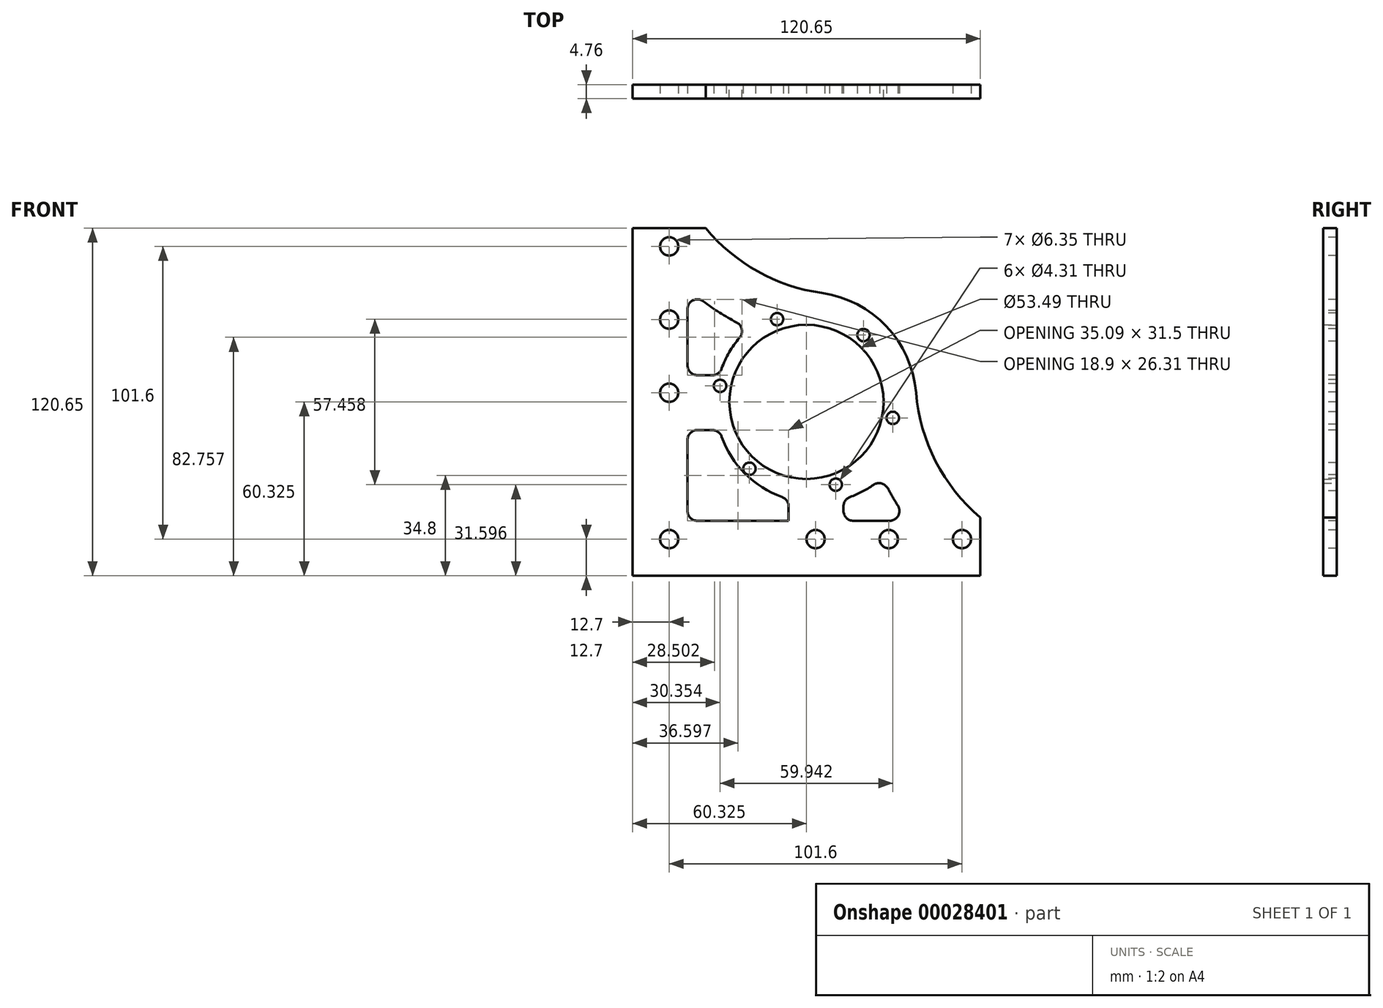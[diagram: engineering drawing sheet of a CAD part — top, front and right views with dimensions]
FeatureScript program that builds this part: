
annotation { "Feature Type Name" : "Feature", "Feature Type Description" : "" }
export const myFeature = defineFeature(function(context is Context, id is Id, definition is map)
    precondition{}
    {
        {
            var Q0;
            Q0=qCreatedBy(makeId("Front.planeOp"),FACE);
            var sketch = newSketch(context, id + "F0", { "sketchPlane" : qUnion([Q0])});
            skLineSegment(sketch, "E0.bottom", {"start": v(0, 0) * mm, "end": v(120.65, 0) * mm});
            skLineSegment(sketch, "E0.top", {"start": v(0, 120.65) * mm, "end": v(25.4, 120.65) * mm});
            skLineSegment(sketch, "E0.left", {"start": v(0, 0) * mm, "end": v(0, 120.65) * mm});
            skLineSegment(sketch, "E0.right", {"start": v(120.65, 0) * mm, "end": v(120.65, 20.24) * mm});
            skCircle(sketch, "E1", {"center": v(60.32, 60.33) * mm, "radius": 26.75 * mm});
            skArc(sketch, "E2", {"start": v(98.37, 63.48) * mm, "mid": v(88.07, 86.55) * mm, "end": v(65.62, 98.13) * mm});
            skArc(sketch, "E3", {"start": v(25.4, 120.65) * mm, "mid": v(43.4, 105.61) * mm, "end": v(65.62, 98.13) * mm});
            skArc(sketch, "E4", {"start": v(98.37, 63.48) * mm, "mid": v(105.2, 39.64) * mm, "end": v(120.65, 20.24) * mm});
            skSolve(sketch);
        }
        {
            var Q0;
            Q0=makeQuery(id+"F0.imprint","IMPRINT",FACE,{"disambiguationData":[TD([[makeQuery(id+"F0.imprint","IMPRINT",EDGE,{"derivedFrom":sQuery(id+"F0.wireOp",EDGE,"E0.bottom")}),1.0]])]});
            var Q1;
            Q1=makeQuery(id+"F0.imprint","IMPRINT",FACE,{"disambiguationData":[TD([[makeQuery(id+"F0.imprint","IMPRINT",EDGE,{"derivedFrom":sQuery(id+"F0.wireOp",EDGE,"E1")}),-1.0]])]});
            extrude(context, id + "F1", {"entities" : qUnion([Q0, Q1]), "depth" : 4.76 * mm});
        }
        {
            var Q0;
            Q0=makeQuery(id+"F1.opExtrude","CAP_FACE",FACE,{"disambiguationData":[OSD([sQuery(id+"F0.wireOp",EDGE,"E0.bottom"),sQuery(id+"F0.wireOp",EDGE,"E0.top"),sQuery(id+"F0.wireOp",EDGE,"E0.left"),sQuery(id+"F0.wireOp",EDGE,"E0.right"),sQuery(id+"F0.wireOp",EDGE,"E1"),sQuery(id+"F0.wireOp",EDGE,"E2"),sQuery(id+"F0.wireOp",EDGE,"E3"),sQuery(id+"F0.wireOp",EDGE,"E4")])],"isStart":false});
            var sketch = newSketch(context, id + "F2", { "sketchPlane" : qUnion([Q0])});
            skLineSegment(sketch, "E5.0", {"start": v(17.11, 101.6) * mm, "end": v(19.05, 101.6) * mm});
            skLineSegment(sketch, "E5.1", {"start": v(19.05, 19.05) * mm, "end": v(19.05, 50.55) * mm});
            skLineSegment(sketch, "E5.2", {"start": v(19.05, 19.05) * mm, "end": v(54.14, 19.05) * mm});
            skArc(sketch, "E5.3", {"start": v(86.76, 34) * mm, "mid": v(90.84, 26.3) * mm, "end": v(95.72, 19.05) * mm});
            skArc(sketch, "E5.5", {"start": v(17.11, 101.6) * mm, "mid": v(28.02, 92.74) * mm, "end": v(40.27, 85.86) * mm});
            skArc(sketch, "E6", {"start": v(73.2, 26.58) * mm, "mid": v(80.4, 29.53) * mm, "end": v(86.76, 34) * mm});
            skLineSegment(sketch, "E7.bottom", {"start": v(19.05, 69.6) * mm, "end": v(30.17, 69.6) * mm});
            skLineSegment(sketch, "E7.top", {"start": v(19.05, 50.55) * mm, "end": v(30.17, 50.55) * mm});
            skLineSegment(sketch, "E8.left", {"start": v(54.14, 26.58) * mm, "end": v(54.14, 19.05) * mm});
            skLineSegment(sketch, "E8.right", {"start": v(73.2, 26.58) * mm, "end": v(73.2, 19.05) * mm});
            skLineSegment(sketch, "E9.trimOffspring", {"start": v(19.05, 69.6) * mm, "end": v(19.05, 101.6) * mm});
            skArc(sketch, "E10.trimOffspring", {"start": v(30.17, 50.55) * mm, "mid": v(39.04, 35.45) * mm, "end": v(54.14, 26.58) * mm});
            skLineSegment(sketch, "E11.trimOffspring", {"start": v(73.2, 19.05) * mm, "end": v(95.72, 19.05) * mm});
            skArc(sketch, "E12.trimOffspring", {"start": v(40.27, 85.86) * mm, "mid": v(34.08, 78.44) * mm, "end": v(30.17, 69.6) * mm});
            skLineSegment(sketch, "E13", {"start": v(63.67, 60.08) * mm, "end": v(63.67, -18.33) * mm, "construction": true});
            skLineSegment(sketch, "E14", {"start": v(63.67, 60.08) * mm, "end": v(-21.5, 60.08) * mm, "construction": true});
            skSolve(sketch);
        }
        {
            var Q0;
            {var subQ4=sQuery(id+"F2.wireOp",EDGE,"E7.bottom");Q0=makeQuery(id+"F2.imprint","IMPRINT",FACE,{"disambiguationData":[TD([[makeQuery(id+"F2.imprint","IMPRINT",EDGE,{"derivedFrom":subQ4}),1.0]])]});}
            var Q1;
            Q1=makeQuery(id+"F2.imprint","IMPRINT",FACE,{"disambiguationData":[TD([[makeQuery(id+"F2.imprint","IMPRINT",EDGE,{"derivedFrom":sQuery(id+"F2.wireOp",EDGE,"E5.1")}),-1.0]])]});
            var Q2;
            Q2=makeQuery(id+"F2.imprint","IMPRINT",FACE,{"disambiguationData":[TD([[makeQuery(id+"F2.imprint","IMPRINT",EDGE,{"derivedFrom":sQuery(id+"F2.wireOp",EDGE,"E5.3")}),-1.0]])]});
            extrude(context, id + "F3", {"entities" : qUnion([Q0, Q1, Q2]), "operationType" : NewBodyOperationType.REMOVE, "endBound" : BoundingType.THROUGH_ALL, "oppositeDirection" : true, "depth" : 25.4 * mm});
        }
        {
            var Q0;
            Q0=makeQuery(id+"F3.boolean.opBoolean","COPY",EDGE,{"derivedFrom":makeQuery(id+"F3.opExtrude","SWEPT_EDGE",EDGE,{"disambiguationData":[OSD([sQuery(id+"F2.wireOp",EDGE,"E5.5"),sQuery(id+"F2.wireOp",EDGE,"E9.trimOffspring")])]})});
            var Q1;
            Q1=makeQuery(id+"F3.boolean.opBoolean","COPY",EDGE,{"derivedFrom":makeQuery(id+"F3.opExtrude","SWEPT_EDGE",EDGE,{"disambiguationData":[OSD([sQuery(id+"F2.wireOp",EDGE,"E7.bottom"),sQuery(id+"F2.wireOp",EDGE,"E9.trimOffspring")])]})});
            var Q2;
            Q2=makeQuery(id+"F3.boolean.opBoolean","COPY",EDGE,{"derivedFrom":makeQuery(id+"F3.opExtrude","SWEPT_EDGE",EDGE,{"disambiguationData":[OSD([sQuery(id+"F2.wireOp",EDGE,"E7.bottom"),sQuery(id+"F2.wireOp",EDGE,"E12.trimOffspring")])]})});
            var Q3;
            Q3=makeQuery(id+"F3.boolean.opBoolean","COPY",EDGE,{"derivedFrom":makeQuery(id+"F3.opExtrude","SWEPT_EDGE",EDGE,{"disambiguationData":[OSD([sQuery(id+"F2.wireOp",EDGE,"E5.5"),sQuery(id+"F2.wireOp",EDGE,"E12.trimOffspring")])]})});
            var Q4;
            Q4=makeQuery(id+"F3.boolean.opBoolean","COPY",EDGE,{"derivedFrom":makeQuery(id+"F3.opExtrude","SWEPT_EDGE",EDGE,{"disambiguationData":[OSD([sQuery(id+"F2.wireOp",EDGE,"E8.left"),sQuery(id+"F2.wireOp",EDGE,"E10.trimOffspring")])]})});
            var Q5;
            Q5=makeQuery(id+"F3.boolean.opBoolean","COPY",EDGE,{"derivedFrom":makeQuery(id+"F3.opExtrude","SWEPT_EDGE",EDGE,{"disambiguationData":[OSD([sQuery(id+"F2.wireOp",EDGE,"E7.top"),sQuery(id+"F2.wireOp",EDGE,"E10.trimOffspring")])]})});
            var Q6;
            Q6=makeQuery(id+"F3.boolean.opBoolean","COPY",EDGE,{"derivedFrom":makeQuery(id+"F3.opExtrude","SWEPT_EDGE",EDGE,{"disambiguationData":[OSD([sQuery(id+"F2.wireOp",EDGE,"E5.1"),sQuery(id+"F2.wireOp",EDGE,"E7.top")])]})});
            var Q7;
            Q7=makeQuery(id+"F3.boolean.opBoolean","COPY",EDGE,{"derivedFrom":makeQuery(id+"F3.opExtrude","SWEPT_EDGE",EDGE,{"disambiguationData":[OSD([sQuery(id+"F2.wireOp",EDGE,"E5.1"),sQuery(id+"F2.wireOp",EDGE,"E5.2")])]})});
            var Q8;
            Q8=makeQuery(id+"F3.boolean.opBoolean","COPY",EDGE,{"derivedFrom":makeQuery(id+"F3.opExtrude","SWEPT_EDGE",EDGE,{"disambiguationData":[OSD([sQuery(id+"F2.wireOp",EDGE,"E6"),sQuery(id+"F2.wireOp",EDGE,"E8.right")])]})});
            var Q9;
            Q9=makeQuery(id+"F3.boolean.opBoolean","COPY",EDGE,{"derivedFrom":makeQuery(id+"F3.opExtrude","SWEPT_EDGE",EDGE,{"disambiguationData":[OSD([sQuery(id+"F2.wireOp",EDGE,"E8.right"),sQuery(id+"F2.wireOp",EDGE,"E11.trimOffspring")])]})});
            var Q10;
            Q10=makeQuery(id+"F3.boolean.opBoolean","COPY",EDGE,{"derivedFrom":makeQuery(id+"F3.opExtrude","SWEPT_EDGE",EDGE,{"disambiguationData":[OSD([sQuery(id+"F2.wireOp",EDGE,"E5.3"),sQuery(id+"F2.wireOp",EDGE,"E6")])]})});
            var Q11;
            Q11=makeQuery(id+"F3.boolean.opBoolean","COPY",EDGE,{"derivedFrom":makeQuery(id+"F3.opExtrude","SWEPT_EDGE",EDGE,{"disambiguationData":[OSD([sQuery(id+"F2.wireOp",EDGE,"E5.3"),sQuery(id+"F2.wireOp",EDGE,"E11.trimOffspring")])]})});
            fillet(context, id + "F4", {"entities" : qUnion([Q0, Q1, Q2, Q3, Q4, Q5, Q6, Q7, Q8, Q9, Q10, Q11]), "radius" : 3.43 * mm, "tangentPropagation" : true, "allowEdgeOverflow" : false});
        }
        {
            var Q0;
            Q0=makeQuery(id+"F1.opExtrude","CAP_FACE",FACE,{"disambiguationData":[OSD([sQuery(id+"F0.wireOp",EDGE,"E0.bottom"),sQuery(id+"F0.wireOp",EDGE,"E0.top"),sQuery(id+"F0.wireOp",EDGE,"E0.left"),sQuery(id+"F0.wireOp",EDGE,"E0.right"),sQuery(id+"F0.wireOp",EDGE,"E1"),sQuery(id+"F0.wireOp",EDGE,"E2"),sQuery(id+"F0.wireOp",EDGE,"E3"),sQuery(id+"F0.wireOp",EDGE,"E4")])],"isStart":false});
            var sketch = newSketch(context, id + "F5", { "sketchPlane" : qUnion([Q0])});
            skLineSegment(sketch, "E15", {"start": v(60.33, 60.33) * mm, "end": v(-15.9, 60.33) * mm, "construction": true});
            skLineSegment(sketch, "E16", {"start": v(60.32, 60.33) * mm, "end": v(60.32, -20.7) * mm, "construction": true});
            skLineSegment(sketch, "E17", {"start": v(12.7, 114.3) * mm, "end": v(12.7, 12.7) * mm, "construction": true});
            skLineSegment(sketch, "E18", {"start": v(12.7, 12.7) * mm, "end": v(114.3, 12.7) * mm, "construction": true});
            skPoint(sketch, "E19", {"position": v(12.7, 88.9) * mm});
            skPoint(sketch, "E20", {"position": v(12.7, 63.5) * mm});
            skPoint(sketch, "E21", {"position": v(88.9, 12.7) * mm});
            skPoint(sketch, "E22", {"position": v(63.5, 12.7) * mm});
            skSolve(sketch);
        }
        {
            var Q0;
            Q0=sQuery(id+"F5.wireOp",VERTEX,"E17.start");
            var Q1;
            Q1=sQuery(id+"F5.wireOp",VERTEX,"E19");
            var Q2;
            Q2=sQuery(id+"F5.wireOp",VERTEX,"E20");
            var Q3;
            Q3=sQuery(id+"F5.wireOp",VERTEX,"E18.start");
            var Q4;
            Q4=sQuery(id+"F5.wireOp",VERTEX,"E22");
            var Q5;
            Q5=sQuery(id+"F5.wireOp",VERTEX,"E21");
            var Q6;
            Q6=sQuery(id+"F5.wireOp",VERTEX,"E18.end");
            var Q7;
            Q7=makeQuery(id+"F1.opExtrude","SWEPT_BODY",BODY,{"disambiguationData":[OSD([sQuery(id+"F0.wireOp",EDGE,"E0.bottom"),sQuery(id+"F0.wireOp",EDGE,"E0.top"),sQuery(id+"F0.wireOp",EDGE,"E0.left"),sQuery(id+"F0.wireOp",EDGE,"E0.right"),sQuery(id+"F0.wireOp",EDGE,"E1"),sQuery(id+"F0.wireOp",EDGE,"E2"),sQuery(id+"F0.wireOp",EDGE,"E3"),sQuery(id+"F0.wireOp",EDGE,"E4")])]});
            hole(context, id + "F6", {"style" : HoleStyle.SIMPLE, "holeDiameter" : 6.35 * mm, "endStyle" : HoleEndStyle.THROUGH, "locations" : qUnion([Q0, Q1, Q2, Q3, Q4, Q5, Q6]), "scope" : qUnion([Q7])});
        }
        {
            var Q0;
            Q0=makeQuery(id+"F1.opExtrude","CAP_FACE",FACE,{"disambiguationData":[OSD([sQuery(id+"F0.wireOp",EDGE,"E0.bottom"),sQuery(id+"F0.wireOp",EDGE,"E0.top"),sQuery(id+"F0.wireOp",EDGE,"E0.left"),sQuery(id+"F0.wireOp",EDGE,"E0.right"),sQuery(id+"F0.wireOp",EDGE,"E1"),sQuery(id+"F0.wireOp",EDGE,"E2"),sQuery(id+"F0.wireOp",EDGE,"E3"),sQuery(id+"F0.wireOp",EDGE,"E4")])],"isStart":false});
            var sketch = newSketch(context, id + "F7", { "sketchPlane" : qUnion([Q0])});
            skCircle(sketch, "E23.cCircle", {"center": v(60.32, 60.33) * mm, "radius": 30.48 * mm, "construction": true});
            skLineSegment(sketch, "E23.0", {"start": v(80.11, 83.5) * mm, "end": v(90.3, 54.78) * mm});
            skLineSegment(sketch, "E23.1", {"start": v(90.3, 54.78) * mm, "end": v(70.5, 31.6) * mm});
            skLineSegment(sketch, "E23.2", {"start": v(70.5, 31.6) * mm, "end": v(40.54, 37.14) * mm});
            skLineSegment(sketch, "E23.3", {"start": v(40.54, 37.14) * mm, "end": v(30.35, 65.87) * mm});
            skLineSegment(sketch, "E23.4", {"start": v(30.35, 65.87) * mm, "end": v(50.14, 89.05) * mm});
            skLineSegment(sketch, "E23.5", {"start": v(50.14, 89.05) * mm, "end": v(80.11, 83.5) * mm});
            skSolve(sketch);
        }
        {
            var Q0;
            Q0=sQuery(id+"F7.wireOp",VERTEX,"E23.4.end");
            var Q1;
            Q1=sQuery(id+"F7.wireOp",VERTEX,"E23.0.start");
            var Q2;
            Q2=sQuery(id+"F7.wireOp",VERTEX,"E23.1.start");
            var Q3;
            Q3=sQuery(id+"F7.wireOp",VERTEX,"E23.2.start");
            var Q4;
            Q4=sQuery(id+"F7.wireOp",VERTEX,"E23.3.start");
            var Q5;
            Q5=sQuery(id+"F7.wireOp",VERTEX,"E23.3.end");
            var Q6;
            Q6=makeQuery(id+"F1.opExtrude","SWEPT_BODY",BODY,{"disambiguationData":[OSD([sQuery(id+"F0.wireOp",EDGE,"E0.bottom"),sQuery(id+"F0.wireOp",EDGE,"E0.top"),sQuery(id+"F0.wireOp",EDGE,"E0.left"),sQuery(id+"F0.wireOp",EDGE,"E0.right"),sQuery(id+"F0.wireOp",EDGE,"E1"),sQuery(id+"F0.wireOp",EDGE,"E2"),sQuery(id+"F0.wireOp",EDGE,"E3"),sQuery(id+"F0.wireOp",EDGE,"E4")])]});
            hole(context, id + "F8", {"style" : HoleStyle.SIMPLE, "holeDiameter" : 4.3 * mm, "endStyle" : HoleEndStyle.THROUGH, "locations" : qUnion([Q0, Q1, Q2, Q3, Q4, Q5]), "scope" : qUnion([Q6])});
        }
    });
